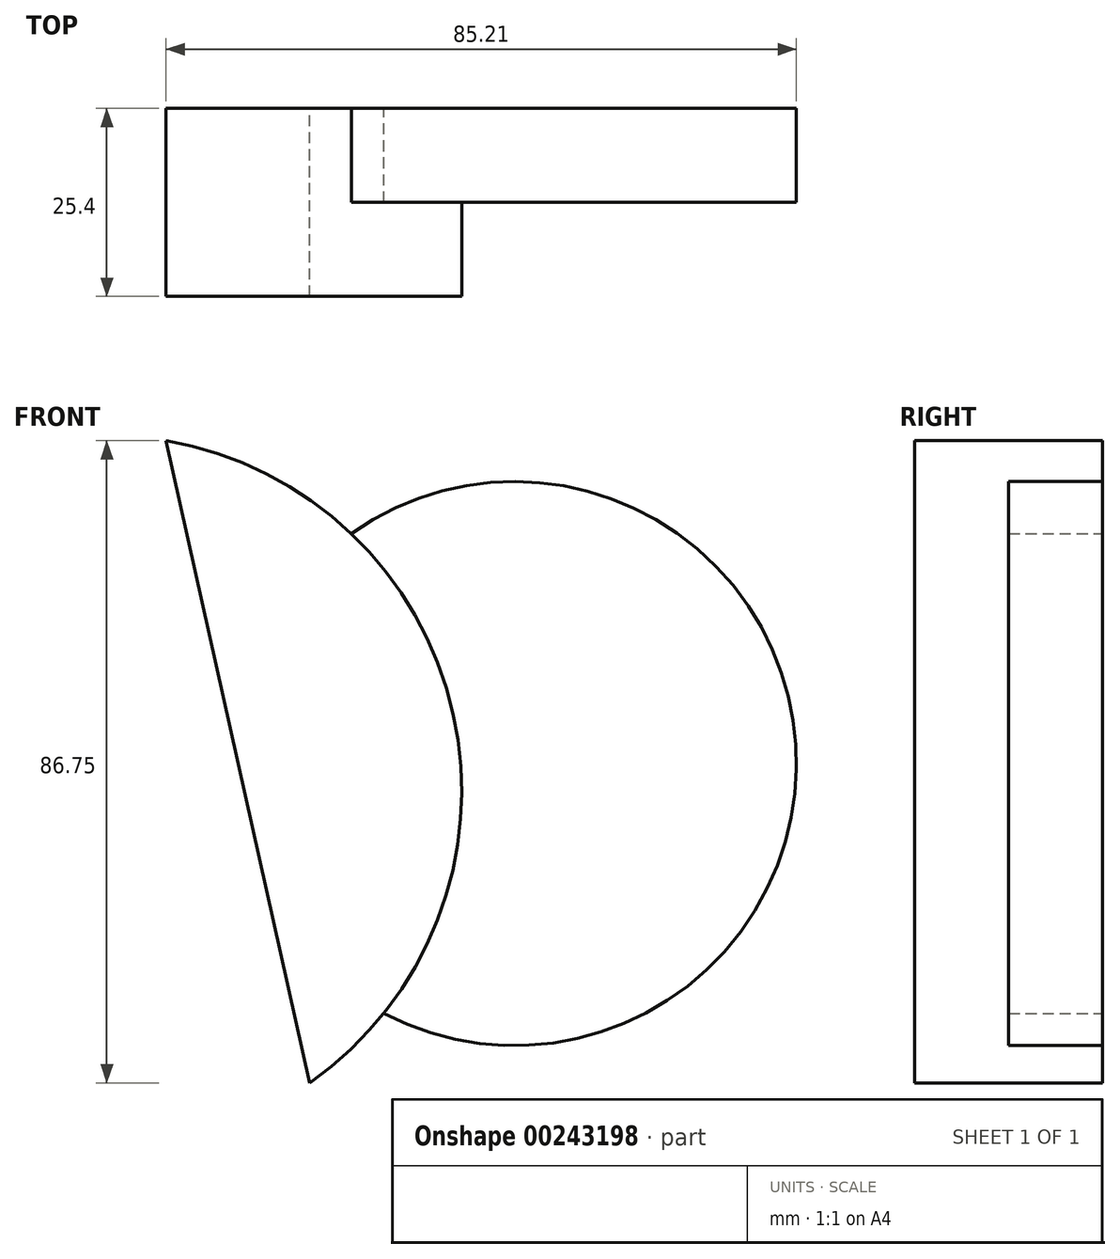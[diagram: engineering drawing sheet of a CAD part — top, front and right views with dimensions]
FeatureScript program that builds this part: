
annotation { "Feature Type Name" : "Feature", "Feature Type Description" : "" }
export const myFeature = defineFeature(function(context is Context, id is Id, definition is map)
    precondition{}
    {
        {
            var Q0;
            Q0=qCreatedBy(makeId("Front.planeOp"),FACE);
            var sketch = newSketch(context, id + "F0", { "sketchPlane" : qUnion([Q0])});
            skCircle(sketch, "E0", {"center": v(0, 0) * mm, "radius": 38.1 * mm});
            skPoint(sketch, "E1", {"position": v(-47.11, 43.61) * mm});
            skPoint(sketch, "E2", {"position": v(-27.7, -43.14) * mm});
            skLineSegment(sketch, "E3", {"start": v(-47.11, 43.61) * mm, "end": v(-27.7, -43.14) * mm});
            skPoint(sketch, "E4", {"position": v(-9.01, 9.5) * mm});
            skCircle(sketch, "E5", {"center": v(-55.2, -3.75) * mm, "radius": 48.05 * mm});
            skLineSegment(sketch, "E6", {"start": v(-47.11, 43.61) * mm, "end": v(-9.01, 43.61) * mm});
            skLineSegment(sketch, "E7", {"start": v(-9.01, 43.61) * mm, "end": v(-9.01, 9.5) * mm});
            skSolve(sketch);
        }
        {
            var Q0;
            {var subQ0=sQuery(id+"F0.wireOp",EDGE,"E3");var subQ1=sQuery(id+"F0.wireOp",EDGE,"E0");var subQ2=makeQuery(id+"F0.imprint","INTERSECT",VERTEX,{"disambiguationData":[OD(0.0)],"derivedFrom":[subQ1,subQ0]});Q0=makeQuery(id+"F0.imprint","IMPRINT",FACE,{"disambiguationData":[TD([[makeQuery(id+"F0.imprint","IMPRINT",EDGE,{"disambiguationData":[TD([[subQ2,-1.0]])],"derivedFrom":subQ1}),-1.0]])]});}
            var Q1;
            {var subQ0=sQuery(id+"F0.wireOp",EDGE,"E5");var subQ1=sQuery(id+"F0.wireOp",EDGE,"E0");var subQ2=makeQuery(id+"F0.imprint","INTERSECT",VERTEX,{"disambiguationData":[OD(1.0)],"derivedFrom":[subQ1,subQ0]});Q1=makeQuery(id+"F0.imprint","IMPRINT",FACE,{"disambiguationData":[TD([[makeQuery(id+"F0.imprint","IMPRINT",EDGE,{"disambiguationData":[TD([[subQ2,-1.0]])],"derivedFrom":subQ1}),-1.0]])]});}
            var Q2;
            {var subQ0=sQuery(id+"F0.wireOp",EDGE,"E5");var subQ2=sQuery(id+"F0.wireOp",EDGE,"E0");var subQ3=makeQuery(id+"F0.imprint","INTERSECT",VERTEX,{"disambiguationData":[OD(1.0)],"derivedFrom":[subQ2,subQ0]});Q2=makeQuery(id+"F0.imprint","IMPRINT",FACE,{"disambiguationData":[TD([[makeQuery(id+"F0.imprint","IMPRINT",EDGE,{"disambiguationData":[TD([[subQ3,-1.0]])],"derivedFrom":subQ2}),1.0]])]});}
            var Q3;
            {var subQ0=sQuery(id+"F0.wireOp",EDGE,"E5");var subQ1=sQuery(id+"F0.wireOp",EDGE,"E0");var subQ2=makeQuery(id+"F0.imprint","INTERSECT",VERTEX,{"disambiguationData":[OD(0.0)],"derivedFrom":[subQ1,subQ0]});Q3=makeQuery(id+"F0.imprint","IMPRINT",FACE,{"disambiguationData":[TD([[makeQuery(id+"F0.imprint","IMPRINT",EDGE,{"disambiguationData":[TD([[subQ2,1.0]])],"derivedFrom":subQ1}),-1.0]])]});}
            var Q4;
            {var subQ0=sQuery(id+"F0.wireOp",EDGE,"E3");var subQ1=sQuery(id+"F0.wireOp",EDGE,"E0");var subQ2=makeQuery(id+"F0.imprint","INTERSECT",VERTEX,{"disambiguationData":[OD(0.0)],"derivedFrom":[subQ1,subQ0]});Q4=makeQuery(id+"F0.imprint","IMPRINT",FACE,{"disambiguationData":[TD([[makeQuery(id+"F0.imprint","IMPRINT",EDGE,{"disambiguationData":[TD([[subQ2,-1.0]])],"derivedFrom":subQ1}),1.0]])]});}
            extrude(context, id + "F1", {"entities" : qUnion([Q0, Q1, Q2, Q3, Q4]), "depth" : 25.4 * mm});
        }
        {
            var Q0;
            {var subQ0=sQuery(id+"F0.wireOp",EDGE,"E5");var subQ2=sQuery(id+"F0.wireOp",EDGE,"E0");var subQ3=makeQuery(id+"F0.imprint","INTERSECT",VERTEX,{"disambiguationData":[OD(1.0)],"derivedFrom":[subQ2,subQ0]});Q0=makeQuery(id+"F0.imprint","IMPRINT",FACE,{"disambiguationData":[TD([[makeQuery(id+"F0.imprint","IMPRINT",EDGE,{"disambiguationData":[TD([[subQ3,-1.0]])],"derivedFrom":subQ2}),1.0]])]});}
            var Q1;
            {var subQ0=sQuery(id+"F0.wireOp",EDGE,"E7");var subQ1=sQuery(id+"F0.wireOp",EDGE,"E0");var subQ2=makeQuery(id+"F0.imprint","INTERSECT",VERTEX,{"derivedFrom":[subQ1,subQ0]});Q1=makeQuery(id+"F0.imprint","IMPRINT",FACE,{"disambiguationData":[TD([[makeQuery(id+"F0.imprint","IMPRINT",EDGE,{"disambiguationData":[TD([[subQ2,-1.0]])],"derivedFrom":subQ1}),1.0]])]});}
            var Q2;
            {var subQ0=sQuery(id+"F0.wireOp",EDGE,"E7");var subQ1=sQuery(id+"F0.wireOp",EDGE,"E0");var subQ2=makeQuery(id+"F0.imprint","INTERSECT",VERTEX,{"derivedFrom":[subQ1,subQ0]});Q2=makeQuery(id+"F0.imprint","IMPRINT",FACE,{"disambiguationData":[TD([[makeQuery(id+"F0.imprint","IMPRINT",EDGE,{"disambiguationData":[TD([[subQ2,1.0]])],"derivedFrom":subQ1}),1.0]])]});}
            var Q3;
            {var subQ0=sQuery(id+"F0.wireOp",EDGE,"E3");var subQ1=sQuery(id+"F0.wireOp",EDGE,"E0");var subQ2=makeQuery(id+"F0.imprint","INTERSECT",VERTEX,{"disambiguationData":[OD(0.0)],"derivedFrom":[subQ1,subQ0]});Q3=makeQuery(id+"F0.imprint","IMPRINT",FACE,{"disambiguationData":[TD([[makeQuery(id+"F0.imprint","IMPRINT",EDGE,{"disambiguationData":[TD([[subQ2,-1.0]])],"derivedFrom":subQ1}),1.0]])]});}
            extrude(context, id + "F2", {"entities" : qUnion([Q0, Q1, Q2, Q3]), "operationType" : NewBodyOperationType.ADD, "depth" : 12.7 * mm});
        }
    });
